# Revit family: MaxlogicAutre Système Module SGC Sortie UART Communication entre le Superviseur
name_source: partatom
category: Fire Alarm Devices
units: mm (PartAtom-declared; Revit-internal decimal feet)

## family parameters
Cut with Voids When Loaded = No
Host = Face
Maintain Annotation Orientation = Yes
OmniClass Number = 23.85.30.21
OmniClass Title = Environmental Detection/Registration
Part Type = Normal
Room Calculation Point = No
Round Connector Dimension = Use Diameter
Shared = No

## types (2) — shared parameters
Adresse ligne 1 = Şerifali Mahallesi Kutup Sokak No:27/1-2-4 Ümraniye TR-34775 İSTANBUL
Alimentation d'externe = 24 V DC
Code de  Performance = EN 54-18
Couleur = Blanc
Deuxime Matèriel = Plastique
Durée de la garantie Travail = 2
Durée de la garantie réservé = 2
Hauteur Nominale = 100 mm
Largeur Nominale = 52 mm
Longeur Nominale = 100 mm
Manuel d'installation = https://mavilielektronik.com
Manufacturer = Mavili Elektronik Ticaret A.Ş.
Matériel Principe = Plastique Blanche PC/ABS
Model = MaxLogic
Numèro de Fax = (+)90 216 466 45 10
Poids = 155 gr
Surface de Montage = Montage à Mur
Tempèrature de Fonctionnement = (-10°C) - (+55°C)
URL = https://www.mavili.com.tr
Unité de durée de garantie = Ans
Voltage de fonctionnement (default) = 26 V/DC
voltage fonction d'opération = 18-33V/DC
zero-valued in all types: Cost, Default Elevation

## per-type parameters (varying)
| type | Code de Produit | Description |
| MaxlogicAutre Système Module SGC, Sortie de TCP/IPı | ML-12012.C | Autre Système Module SGC, Sortie de TCP/IP |
| Maxlogic Autre Système Module SGC Sortie UART Communication entre le Superviseur (Câble Inclus) | ML-12012.UART | Autre Système Module SGC Sortie UART Communication entre le Superviseur (Câble Inclus) |

## geometry (parser evidence)
native form markers: Sweep x2
no freeform markers — native parametric forms only
